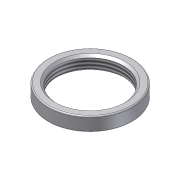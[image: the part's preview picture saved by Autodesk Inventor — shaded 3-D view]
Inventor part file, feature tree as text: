
AUTODESK INVENTOR PART (.ipt)
format: ipt  version: 2013 (Build 170138000, 138)  size: 99,840 bytes
history: native  units: mm (DEFAULTED — no unit token found)
features: extrude x1, thread x1, chamfer x1, fillet x1, sketch x1
ambient origin geometry x8: Origin, YZ Plane, XZ Plane, XY Plane, X Axis, Y Axis, Z Axis, Center Point
bodies: Solid1 (feature_tree)
feature tree (5):
  extrude  "Extrusion1"  Depth=29.0mm
  thread  "Thread1"  [1 undecoded]
  chamfer  "Chamfer1"  Distance=0.5mm
  fillet  "Fillet1"  [1 undecoded]
  sketch  "Sketch1"  dims[d0=37.0mm d1=29.0mm d2=6.2mm d3=0.0mm d4=10.0mm d5=0.0mm d6=1.0mm d7=2.0mm d8=45.0deg d9=0.5mm]
note: 2 required parameter values undecoded (feature->parameter linkage not recoverable at this tier; creation-order binding heuristic only, values carry confidence <= 0.55)
